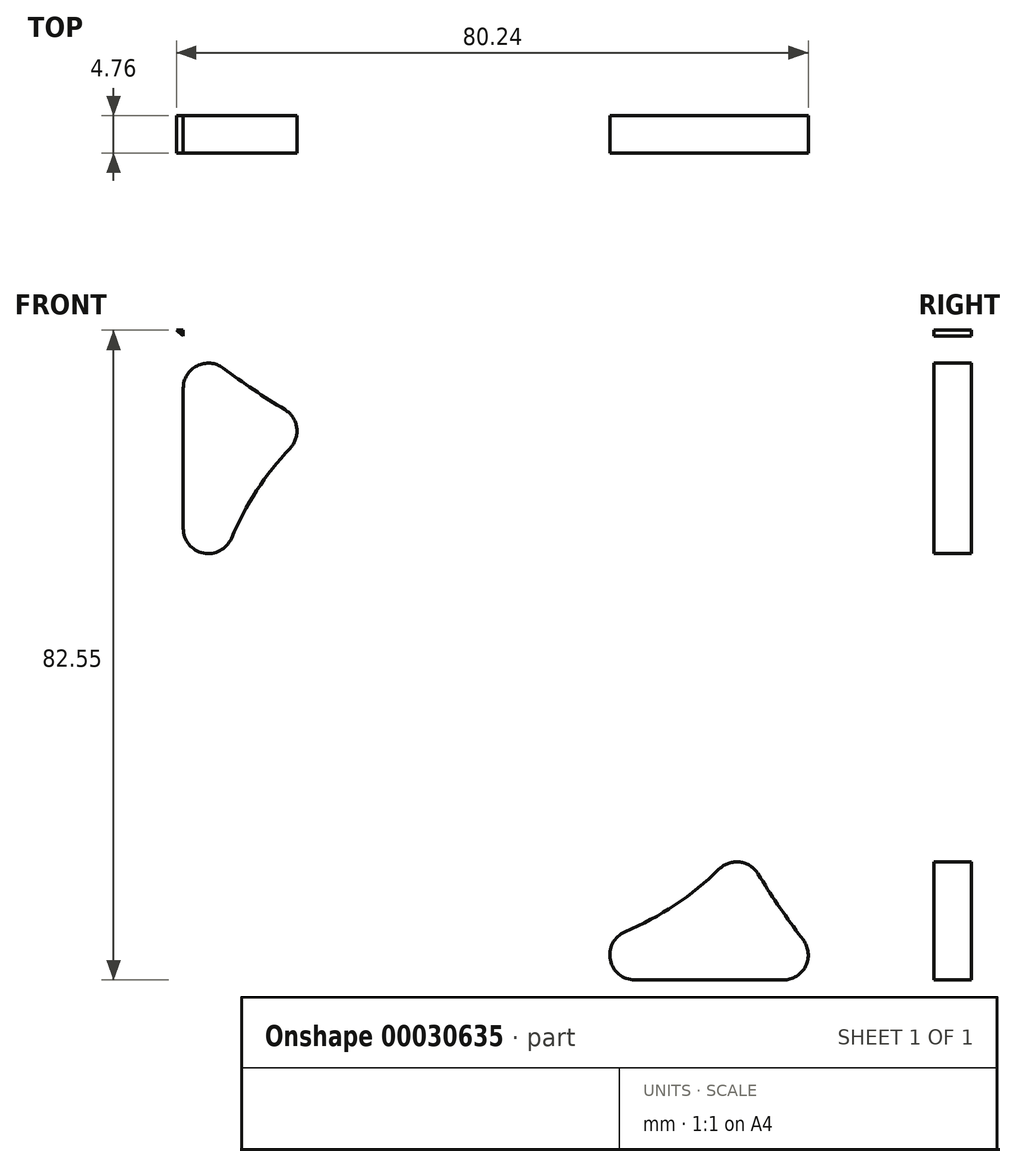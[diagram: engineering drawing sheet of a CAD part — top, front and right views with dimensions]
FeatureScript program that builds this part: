
annotation { "Feature Type Name" : "Feature", "Feature Type Description" : "" }
export const myFeature = defineFeature(function(context is Context, id is Id, definition is map)
    precondition{}
    {
        {
            var Q0;
            Q0=qCreatedBy(makeId("Front.planeOp"),FACE);
            var sketch = newSketch(context, id + "F0", { "sketchPlane" : qUnion([Q0])});
            skLineSegment(sketch, "E0.bottom", {"start": v(-45.53, 63.86) * mm, "end": v(-20.13, 63.86) * mm});
            skLineSegment(sketch, "E0.top", {"start": v(-45.53, -56.8) * mm, "end": v(75.12, -56.8) * mm});
            skLineSegment(sketch, "E0.left", {"start": v(-45.53, 63.86) * mm, "end": v(-45.53, -56.8) * mm});
            skLineSegment(sketch, "E0.right", {"start": v(75.12, -31.4) * mm, "end": v(75.12, -56.8) * mm});
            skLineSegment(sketch, "E1", {"start": v(-32.83, 63.86) * mm, "end": v(-32.83, -56.8) * mm, "construction": true});
            skLineSegment(sketch, "E2", {"start": v(-45.53, -44.1) * mm, "end": v(75.12, -44.1) * mm, "construction": true});
            skCircle(sketch, "E3", {"center": v(-32.83, -44.1) * mm, "radius": 3.18 * mm});
            skCircle(sketch, "E4", {"center": v(-32.83, 6.7) * mm, "radius": 3.18 * mm});
            skCircle(sketch, "E5", {"center": v(-32.83, 32.1) * mm, "radius": 3.18 * mm});
            skCircle(sketch, "E6", {"center": v(-32.83, 57.5) * mm, "radius": 3.18 * mm});
            skCircle(sketch, "E7", {"center": v(17.97, -44.1) * mm, "radius": 3.18 * mm});
            skCircle(sketch, "E8", {"center": v(43.37, -44.1) * mm, "radius": 3.18 * mm});
            skCircle(sketch, "E9", {"center": v(68.77, -44.1) * mm, "radius": 3.18 * mm});
            skCircle(sketch, "E10", {"center": v(14.8, 3.53) * mm, "radius": 26.75 * mm});
            skCircle(sketch, "E11", {"center": v(14.8, 3.53) * mm, "radius": 30.48 * mm, "construction": true});
            skArc(sketch, "E12", {"start": v(51.47, 14.14) * mm, "mid": v(43.53, 28.67) * mm, "end": v(30.18, 38.47) * mm});
            skLineSegment(sketch, "E13", {"start": v(-45.53, -56.8) * mm, "end": v(14.8, 3.53) * mm, "construction": true});
            skLineSegment(sketch, "E14", {"start": v(14.8, 3.53) * mm, "end": v(2.23, -43.37) * mm, "construction": true});
            skLineSegment(sketch, "E15.0", {"start": v(6.91, -25.9) * mm, "end": v(-14.64, -4.35) * mm, "construction": true});
            skLineSegment(sketch, "E15.1", {"start": v(-14.64, -4.35) * mm, "end": v(-6.75, 25.09) * mm, "construction": true});
            skLineSegment(sketch, "E15.2", {"start": v(-6.75, 25.09) * mm, "end": v(22.69, 32.98) * mm, "construction": true});
            skLineSegment(sketch, "E15.3", {"start": v(22.69, 32.98) * mm, "end": v(44.24, 11.42) * mm, "construction": true});
            skLineSegment(sketch, "E15.4", {"start": v(44.24, 11.42) * mm, "end": v(36.35, -18.02) * mm, "construction": true});
            skLineSegment(sketch, "E15.5", {"start": v(36.35, -18.02) * mm, "end": v(6.91, -25.9) * mm, "construction": true});
            skCircle(sketch, "E16", {"center": v(22.69, 32.98) * mm, "radius": 2.15 * mm});
            skCircle(sketch, "E17", {"center": v(6.91, -25.9) * mm, "radius": 2.15 * mm});
            skCircle(sketch, "E18", {"center": v(-14.64, -4.35) * mm, "radius": 2.15 * mm});
            skCircle(sketch, "E19", {"center": v(-6.75, 25.09) * mm, "radius": 2.15 * mm});
            skCircle(sketch, "E20", {"center": v(44.24, 11.42) * mm, "radius": 2.15 * mm});
            skCircle(sketch, "E21", {"center": v(36.35, -18.02) * mm, "radius": 2.15 * mm});
            skLineSegment(sketch, "E22", {"start": v(-20.13, 63.86) * mm, "end": v(-0.83, 46.83) * mm});
            skLineSegment(sketch, "E23", {"start": v(-0.83, 46.83) * mm, "end": v(24.12, 40.56) * mm});
            skLineSegment(sketch, "E24", {"start": v(75.12, -31.4) * mm, "end": v(59.22, -10.16) * mm});
            skLineSegment(sketch, "E25", {"start": v(59.22, -10.16) * mm, "end": v(51.18, 15.12) * mm});
            skArc(sketch, "E26.trimOffspring", {"start": v(51.47, 14.14) * mm, "mid": v(41.32, 31) * mm, "end": v(24.12, 40.56) * mm});
            skSolve(sketch);
        }
        {
            var Q0;
            Q0=makeQuery(id+"F0.imprint","IMPRINT",FACE,{"disambiguationData":[TD([[makeQuery(id+"F0.imprint","IMPRINT",EDGE,{"derivedFrom":sQuery(id+"F0.wireOp",EDGE,"E0.bottom")}),-1.0]])]});
            extrude(context, id + "F1", {"entities" : qUnion([Q0]), "depth" : 4.76 * mm});
        }
        {
            var Q0;
            Q0=makeQuery(id+"F1.opExtrude","SWEPT_EDGE",EDGE,{"disambiguationData":[OSD([sQuery(id+"F0.wireOp",EDGE,"E22"),sQuery(id+"F0.wireOp",EDGE,"E23")])]});
            var Q1;
            Q1=makeQuery(id+"F1.opExtrude","SWEPT_EDGE",EDGE,{"disambiguationData":[OSD([sQuery(id+"F0.wireOp",EDGE,"E24"),sQuery(id+"F0.wireOp",EDGE,"E25")])]});
            fillet(context, id + "F2", {"entities" : qUnion([Q0, Q1]), "radius" : 76.2 * mm, "tangentPropagation" : true, "allowEdgeOverflow" : false});
        }
        {
            var Q0;
            Q0=makeQuery(id+"F1.opExtrude","SWEPT_EDGE",EDGE,{"disambiguationData":[OSD([sQuery(id+"F0.wireOp",EDGE,"E0.bottom"),sQuery(id+"F0.wireOp",EDGE,"E0.left")])]});
            var Q1;
            Q1=makeQuery(id+"F1.opExtrude","SWEPT_EDGE",EDGE,{"disambiguationData":[OSD([sQuery(id+"F0.wireOp",EDGE,"E0.bottom"),sQuery(id+"F0.wireOp",EDGE,"E22")])]});
            var Q2;
            Q2=makeQuery(id+"F1.opExtrude","SWEPT_EDGE",EDGE,{"disambiguationData":[OSD([sQuery(id+"F0.wireOp",EDGE,"E0.top"),sQuery(id+"F0.wireOp",EDGE,"E0.left")])]});
            var Q3;
            Q3=makeQuery(id+"F1.opExtrude","SWEPT_EDGE",EDGE,{"disambiguationData":[OSD([sQuery(id+"F0.wireOp",EDGE,"E0.right"),sQuery(id+"F0.wireOp",EDGE,"E24")])]});
            var Q4;
            Q4=makeQuery(id+"F1.opExtrude","SWEPT_EDGE",EDGE,{"disambiguationData":[OSD([sQuery(id+"F0.wireOp",EDGE,"E0.top"),sQuery(id+"F0.wireOp",EDGE,"E0.right")])]});
            fillet(context, id + "F3", {"entities" : qUnion([Q0, Q1, Q2, Q3, Q4]), "radius" : 3.17 * mm, "tangentPropagation" : true, "allowEdgeOverflow" : false});
        }
        {
            var Q0;
            Q0=makeQuery(id+"F1.opExtrude","CAP_FACE",FACE,{"disambiguationData":[OSD([sQuery(id+"F0.wireOp",EDGE,"E0.bottom"),sQuery(id+"F0.wireOp",EDGE,"E0.top"),sQuery(id+"F0.wireOp",EDGE,"E0.left"),sQuery(id+"F0.wireOp",EDGE,"E0.right"),sQuery(id+"F0.wireOp",EDGE,"E3"),sQuery(id+"F0.wireOp",EDGE,"E4"),sQuery(id+"F0.wireOp",EDGE,"E5"),sQuery(id+"F0.wireOp",EDGE,"E6"),sQuery(id+"F0.wireOp",EDGE,"E7"),sQuery(id+"F0.wireOp",EDGE,"E8"),sQuery(id+"F0.wireOp",EDGE,"E9"),sQuery(id+"F0.wireOp",EDGE,"E10"),sQuery(id+"F0.wireOp",EDGE,"E16"),sQuery(id+"F0.wireOp",EDGE,"E17"),sQuery(id+"F0.wireOp",EDGE,"E18"),sQuery(id+"F0.wireOp",EDGE,"E19"),sQuery(id+"F0.wireOp",EDGE,"E20"),sQuery(id+"F0.wireOp",EDGE,"E21"),sQuery(id+"F0.wireOp",EDGE,"E22"),sQuery(id+"F0.wireOp",EDGE,"E23"),sQuery(id+"F0.wireOp",EDGE,"E24"),sQuery(id+"F0.wireOp",EDGE,"E25"),sQuery(id+"F0.wireOp",EDGE,"E26.trimOffspring")])],"isStart":false});
            var sketch = newSketch(context, id + "F4", { "sketchPlane" : qUnion([Q0])});
            skArc(sketch, "E27.0", {"start": v(-13.57, 34.7) * mm, "mid": v(-17.55, 37.24) * mm, "end": v(-21.4, 39.98) * mm});
            skArc(sketch, "E27.4", {"start": v(51.69, -31.88) * mm, "mid": v(49.02, -28.13) * mm, "end": v(46.54, -24.27) * mm});
            skLineSegment(sketch, "E27.5", {"start": v(-27.32, 44.8) * mm, "end": v(-27.33, 44.8) * mm});
            skLineSegment(sketch, "E27.6", {"start": v(52.28, -32.66) * mm, "end": v(51.69, -31.88) * mm});
            skLineSegment(sketch, "E27.7", {"start": v(56.07, -37.74) * mm, "end": v(56.07, -37.73) * mm});
            skLineSegment(sketch, "E27.8", {"start": v(-23.3, -37.74) * mm, "end": v(-1.27, -37.74) * mm});
            skLineSegment(sketch, "E27.9", {"start": v(-26.48, 44.8) * mm, "end": v(-26.48, 44.06) * mm});
            skLineSegment(sketch, "E27.10", {"start": v(-26.48, 44.8) * mm, "end": v(-27.33, 44.8) * mm});
            skArc(sketch, "E28.0", {"start": v(-12.9, 29.8) * mm, "mid": v(-17.15, 24.42) * mm, "end": v(-20.37, 18.37) * mm});
            skArc(sketch, "E29", {"start": v(-26.48, 19.6) * mm, "mid": v(-23.93, 16.5) * mm, "end": v(-20.37, 18.37) * mm});
            skArc(sketch, "E30", {"start": v(-20.37, -11.3) * mm, "mid": v(-23.93, -9.43) * mm, "end": v(-26.48, -12.54) * mm});
            skArc(sketch, "E31", {"start": v(-1.27, -37.74) * mm, "mid": v(1.84, -35.2) * mm, "end": v(-0.04, -31.64) * mm});
            skArc(sketch, "E32", {"start": v(46.54, -24.27) * mm, "mid": v(44.22, -22.76) * mm, "end": v(41.6, -23.65) * mm});
            skArc(sketch, "E33", {"start": v(49.74, -37.74) * mm, "mid": v(52.58, -35.99) * mm, "end": v(52.28, -32.66) * mm});
            skArc(sketch, "E34", {"start": v(-26.48, -34.57) * mm, "mid": v(-25.55, -36.81) * mm, "end": v(-23.3, -37.74) * mm});
            skArc(sketch, "E35", {"start": v(-12.9, 29.8) * mm, "mid": v(-12.06, 32.4) * mm, "end": v(-13.57, 34.7) * mm});
            skArc(sketch, "E36", {"start": v(-21.4, 39.98) * mm, "mid": v(-24.72, 40.28) * mm, "end": v(-26.48, 37.44) * mm});
            skArc(sketch, "E37", {"start": v(29.64, -31.64) * mm, "mid": v(27.76, -35.2) * mm, "end": v(30.87, -37.74) * mm});
            skLineSegment(sketch, "E38.trimOffspring", {"start": v(-26.48, 37.44) * mm, "end": v(-26.48, 19.6) * mm});
            skArc(sketch, "E39.trimOffspring", {"start": v(-26.48, 44.06) * mm, "mid": v(-26.9, 44.43) * mm, "end": v(-27.32, 44.8) * mm});
            skArc(sketch, "E40.trimOffspring", {"start": v(29.64, -31.64) * mm, "mid": v(36, -28.22) * mm, "end": v(41.6, -23.65) * mm});
            skLineSegment(sketch, "E41.trimOffspring", {"start": v(30.87, -37.74) * mm, "end": v(49.74, -37.74) * mm});
            skLineSegment(sketch, "E42.trimOffspring", {"start": v(-26.48, -12.54) * mm, "end": v(-26.48, -34.57) * mm});
            skArc(sketch, "E43.trimOffspring", {"start": v(-20.37, -11.3) * mm, "mid": v(-12.2, -23.46) * mm, "end": v(-0.04, -31.64) * mm});
            skSolve(sketch);
        }
        {
            var Q0;
            Q0=makeQuery(id+"F4.imprint","IMPRINT",FACE,{"disambiguationData":[TD([[makeQuery(id+"F4.imprint","IMPRINT",EDGE,{"derivedFrom":sQuery(id+"F4.wireOp",EDGE,"E27.0")}),1.0]])]});
            var Q1;
            Q1=makeQuery(id+"F4.imprint","IMPRINT",FACE,{"disambiguationData":[TD([[makeQuery(id+"F4.imprint","IMPRINT",EDGE,{"derivedFrom":sQuery(id+"F4.wireOp",EDGE,"E27.8")}),1.0]])]});
            var Q2;
            Q2=makeQuery(id+"F4.imprint","IMPRINT",FACE,{"disambiguationData":[TD([[makeQuery(id+"F4.imprint","IMPRINT",EDGE,{"derivedFrom":sQuery(id+"F4.wireOp",EDGE,"E27.4")}),1.0]])]});
            extrude(context, id + "F5", {"entities" : qUnion([Q0, Q1, Q2]), "operationType" : NewBodyOperationType.REMOVE, "endBound" : BoundingType.THROUGH_ALL, "oppositeDirection" : true, "depth" : 25.4 * mm});
        }
    });
